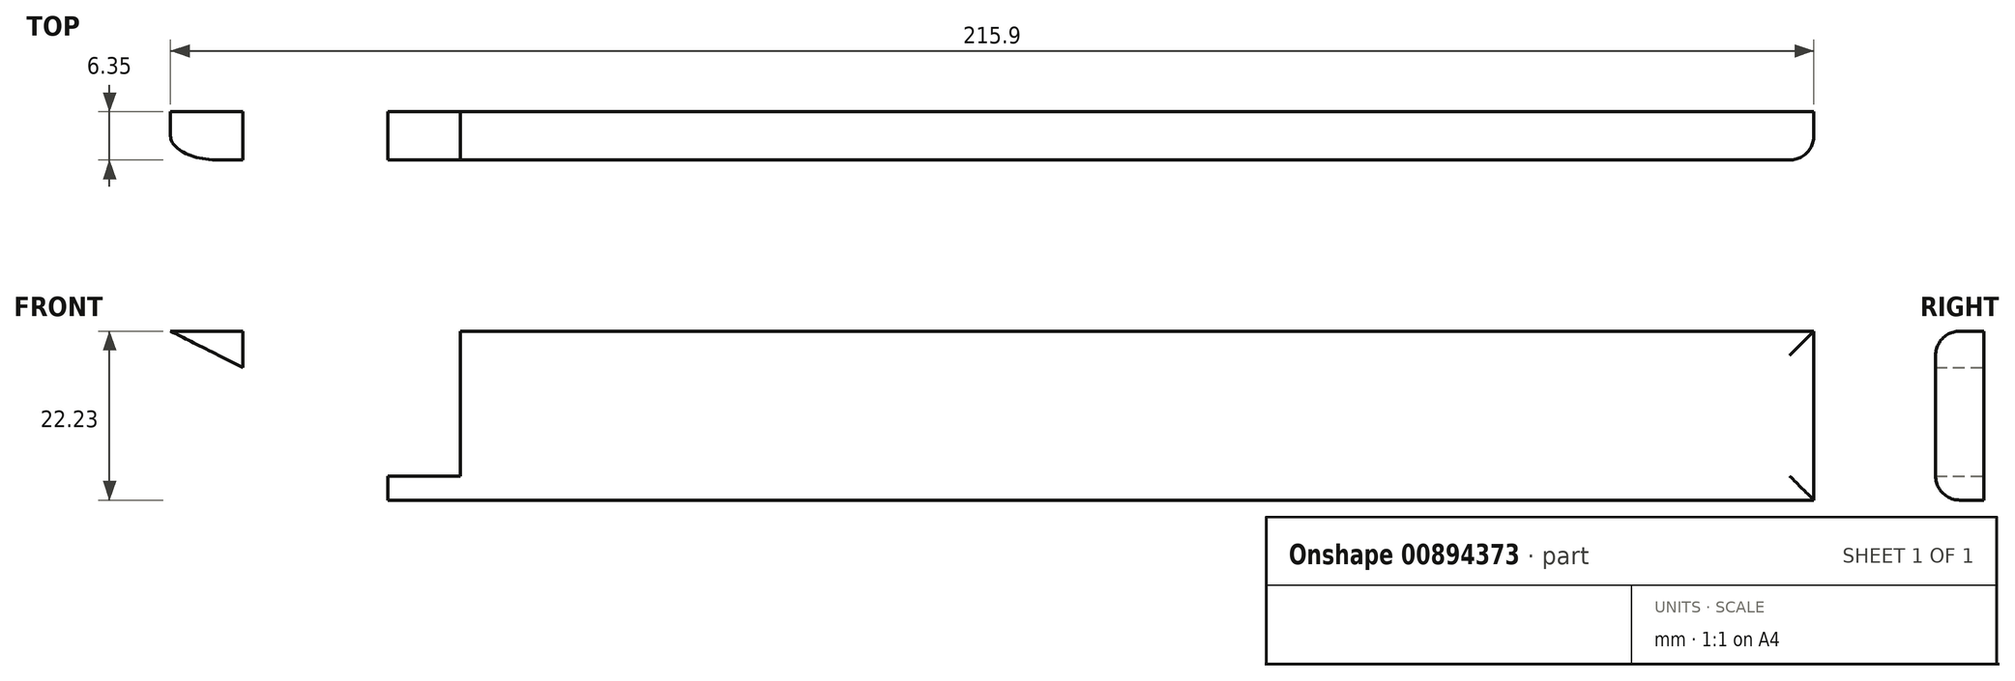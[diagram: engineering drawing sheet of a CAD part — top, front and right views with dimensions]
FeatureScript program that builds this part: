
annotation { "Feature Type Name" : "Feature", "Feature Type Description" : "" }
export const myFeature = defineFeature(function(context is Context, id is Id, definition is map)
    precondition{}
    {
        {
            var Q0;
            Q0=qCreatedBy(makeId("Front.planeOp"),FACE);
            var sketch = newSketch(context, id + "F0", { "sketchPlane" : qUnion([Q0])});
            skLineSegment(sketch, "E0.bottom", {"start": v(47.57, 0.5) * mm, "end": v(225.37, 0.5) * mm});
            skLineSegment(sketch, "E0.top", {"start": v(47.57, 22.73) * mm, "end": v(225.37, 22.73) * mm});
            skLineSegment(sketch, "E0.left", {"start": v(47.57, 0.5) * mm, "end": v(47.57, 22.73) * mm});
            skLineSegment(sketch, "E0.right", {"start": v(225.37, 0.5) * mm, "end": v(225.37, 22.73) * mm});
            skLineSegment(sketch, "E1.bottom", {"start": v(47.57, 0.5) * mm, "end": v(9.47, 0.5) * mm});
            skLineSegment(sketch, "E1.top", {"start": v(47.57, 22.73) * mm, "end": v(9.47, 22.73) * mm});
            skLineSegment(sketch, "E2.left", {"start": v(9.47, 0.5) * mm, "end": v(9.47, -2.42) * mm});
            skLineSegment(sketch, "E2.right", {"start": v(-155.63, 0.5) * mm, "end": v(-155.63, -59.94) * mm});
            skArc(sketch, "E3", {"start": v(9.47, 0.5) * mm, "mid": v(-4.22, -17.23) * mm, "end": v(-11.89, -38.28) * mm});
            skArc(sketch, "E4", {"start": v(-38.43, -17.23) * mm, "mid": v(-28.48, -31.94) * mm, "end": v(-11.89, -38.28) * mm});
            skPoint(sketch, "E4.startSnap0", {"position": v(-4.22, -17.23) * mm});
            skArc(sketch, "E5", {"start": v(9.47, 22.73) * mm, "mid": v(-1.4, 20.26) * mm, "end": v(-10.13, 13.34) * mm});
            skArc(sketch, "E6", {"start": v(-155.63, -59.94) * mm, "mid": v(-95.28, -43.39) * mm, "end": v(-38.43, -17.23) * mm});
            skArc(sketch, "E7", {"start": v(-97.34, 6.63) * mm, "mid": v(-126.55, 4.14) * mm, "end": v(-155.63, 0.5) * mm});
            skArc(sketch, "E8.0", {"start": v(-51.22, -4.45) * mm, "mid": v(-97.17, -6.09) * mm, "end": v(-142.93, -10.57) * mm});
            skArc(sketch, "E8.1", {"start": v(-50.24, -9.24) * mm, "mid": v(-50.54, -6.8) * mm, "end": v(-51.22, -4.45) * mm});
            skArc(sketch, "E8.2", {"start": v(-142.93, -44.3) * mm, "mid": v(-95.4, -29.88) * mm, "end": v(-50.24, -9.24) * mm});
            skLineSegment(sketch, "E8.3", {"start": v(-142.93, -10.57) * mm, "end": v(-142.93, -44.3) * mm});
            skPoint(sketch, "E9", {"position": v(38.04, 3.68) * mm});
            skLineSegment(sketch, "E10", {"start": v(38.04, 3.68) * mm, "end": v(38.04, 0.5) * mm});
            skLineSegment(sketch, "E11", {"start": v(38.04, 3.68) * mm, "end": v(47.57, 3.68) * mm});
            skLineSegment(sketch, "E12", {"start": v(9.47, 22.73) * mm, "end": v(17.79, 22.73) * mm});
            skLineSegment(sketch, "E13", {"start": v(9.47, 22.73) * mm, "end": v(19, 22.73) * mm});
            skLineSegment(sketch, "E14", {"start": v(19, 22.73) * mm, "end": v(19, 17.97) * mm});
            skLineSegment(sketch, "E15", {"start": v(19, 17.97) * mm, "end": v(9.47, 22.73) * mm});
            skFitSpline(sketch, "E16", {"points": [v(-10.13, 13.34) * mm, v(-24.5, 0) * mm, v(-55.64, 8.21) * mm], "startDerivative": vector(-27.78, -40.13) * mm, "endDerivative": vector(-61.83, 26.33) * mm});
            skFitSpline(sketch, "E17", {"points": [v(-40.15, 1.98) * mm, v(-66.13, 8.03) * mm, v(-97.34, 6.63) * mm], "startDerivative": vector(-52.72, 15.41) * mm, "endDerivative": vector(-61.46, -7.14) * mm});
            skSolve(sketch);
        }
        {
            var Q0;
            {var subQ3=sQuery(id+"F0.wireOp",EDGE,"E1.top");Q0=makeQuery(id+"F0.imprint","IMPRINT",FACE,{"disambiguationData":[TD([[makeQuery(id+"F0.imprint","IMPRINT",EDGE,{"derivedFrom":subQ3}),1.0]])]});}
            var Q1;
            {var subQ1=sQuery(id+"F0.wireOp",EDGE,"E0.bottom");Q1=makeQuery(id+"F0.imprint","IMPRINT",FACE,{"disambiguationData":[TD([[makeQuery(id+"F0.imprint","IMPRINT",EDGE,{"derivedFrom":subQ1}),1.0]])]});}
            var Q2;
            {var subQ3=sQuery(id+"F0.wireOp",EDGE,"E10");Q2=makeQuery(id+"F0.imprint","IMPRINT",FACE,{"disambiguationData":[TD([[makeQuery(id+"F0.imprint","IMPRINT",EDGE,{"derivedFrom":subQ3}),1.0]])]});}
            extrude(context, id + "F1", {"entities" : qUnion([Q0, Q1, Q2]), "depth" : 6.35 * mm, "offsetDistance" : 25.4 * mm});
        }
        {
            var Q0;
            Q0=makeQuery(id+"F1.opExtrude","CAP_FACE",FACE,{"disambiguationData":[OSD([sQuery(id+"F0.wireOp",EDGE,"E0.bottom"),sQuery(id+"F0.wireOp",EDGE,"E0.top"),sQuery(id+"F0.wireOp",EDGE,"E0.right"),sQuery(id+"F0.wireOp",EDGE,"E1.bottom"),sQuery(id+"F0.wireOp",EDGE,"E1.top"),sQuery(id+"F0.wireOp",EDGE,"E2.right"),sQuery(id+"F0.wireOp",EDGE,"E3"),sQuery(id+"F0.wireOp",EDGE,"E4"),sQuery(id+"F0.wireOp",EDGE,"E5"),sQuery(id+"F0.wireOp",EDGE,"E6"),sQuery(id+"F0.wireOp",EDGE,"E7"),sQuery(id+"F0.wireOp",EDGE,"E8.0"),sQuery(id+"F0.wireOp",EDGE,"E8.1"),sQuery(id+"F0.wireOp",EDGE,"E8.2"),sQuery(id+"F0.wireOp",EDGE,"E8.3"),sQuery(id+"F0.wireOp",EDGE,"E14"),sQuery(id+"F0.wireOp",EDGE,"E15"),sQuery(id+"F0.wireOp",EDGE,"E16"),sQuery(id+"F0.wireOp",EDGE,"E17")])],"isStart":false});
            var sketch = newSketch(context, id + "F2", { "sketchPlane" : qUnion([Q0])});
            skLineSegment(sketch, "E18", {"start": v(9.47, 0.5) * mm, "end": v(47.57, 0.5) * mm});
            skLineSegment(sketch, "E19", {"start": v(47.57, 0.5) * mm, "end": v(47.57, 3.68) * mm});
            skLineSegment(sketch, "E20", {"start": v(47.57, 3.68) * mm, "end": v(38.04, 3.68) * mm});
            skPoint(sketch, "E21", {"position": v(38.04, 3.68) * mm});
            skSolve(sketch);
        }
        {
            var Q0;
            Q0=sQuery(id+"F2.wireOp",VERTEX,"E20.end");
            var Q1;
            Q1=makeQuery(id+"F1.opExtrude","SWEPT_BODY",BODY,{"disambiguationData":[OSD([sQuery(id+"F0.wireOp",EDGE,"E0.bottom"),sQuery(id+"F0.wireOp",EDGE,"E0.top"),sQuery(id+"F0.wireOp",EDGE,"E0.right"),sQuery(id+"F0.wireOp",EDGE,"E1.bottom"),sQuery(id+"F0.wireOp",EDGE,"E1.top"),sQuery(id+"F0.wireOp",EDGE,"E2.right"),sQuery(id+"F0.wireOp",EDGE,"E3"),sQuery(id+"F0.wireOp",EDGE,"E4"),sQuery(id+"F0.wireOp",EDGE,"E5"),sQuery(id+"F0.wireOp",EDGE,"E6"),sQuery(id+"F0.wireOp",EDGE,"E7"),sQuery(id+"F0.wireOp",EDGE,"E8.0"),sQuery(id+"F0.wireOp",EDGE,"E8.1"),sQuery(id+"F0.wireOp",EDGE,"E8.2"),sQuery(id+"F0.wireOp",EDGE,"E8.3"),sQuery(id+"F0.wireOp",EDGE,"E14"),sQuery(id+"F0.wireOp",EDGE,"E15"),sQuery(id+"F0.wireOp",EDGE,"E16"),sQuery(id+"F0.wireOp",EDGE,"E17")])]});
            hole(context, id + "F3", {"style" : HoleStyle.SIMPLE, "endStyle" : HoleEndStyle.BLIND, "holeDiameter" : 2.38 * mm, "majorDiameter" : 6.35 * mm, "holeDepth" : 6.35 * mm, "isTappedThrough" : true, "tappedDepth" : 12.7 * mm, "tapClearance" : 3, "locations" : qUnion([Q0]), "scope" : qUnion([Q1])});
        }
        {
            var Q0;
            Q0=makeQuery(id+"F1.opExtrude","CAP_EDGE",EDGE,{"disambiguationData":[OSD([sQuery(id+"F0.wireOp",EDGE,"E6")])],"isStart":false});
            var Q1;
            Q1=makeQuery(id+"F1.opExtrude","CAP_EDGE",EDGE,{"disambiguationData":[OSD([sQuery(id+"F0.wireOp",EDGE,"E2.right")])],"isStart":false});
            var Q2;
            Q2=makeQuery(id+"F1.opExtrude","CAP_EDGE",EDGE,{"disambiguationData":[OSD([sQuery(id+"F0.wireOp",EDGE,"E7")])],"isStart":false});
            var Q3;
            Q3=makeQuery(id+"F1.opExtrude","CAP_EDGE",EDGE,{"disambiguationData":[OSD([sQuery(id+"F0.wireOp",EDGE,"E8.0")])],"isStart":false});
            var Q4;
            Q4=makeQuery(id+"F1.opExtrude","CAP_EDGE",EDGE,{"disambiguationData":[OSD([sQuery(id+"F0.wireOp",EDGE,"E8.3")])],"isStart":false});
            var Q5;
            Q5=makeQuery(id+"F1.opExtrude","CAP_EDGE",EDGE,{"disambiguationData":[OSD([sQuery(id+"F0.wireOp",EDGE,"E8.2")])],"isStart":false});
            var Q6;
            Q6=makeQuery(id+"F1.opExtrude","CAP_EDGE",EDGE,{"disambiguationData":[OSD([sQuery(id+"F0.wireOp",EDGE,"E8.1")])],"isStart":false});
            var Q7;
            Q7=makeQuery(id+"F1.opExtrude","CAP_EDGE",EDGE,{"disambiguationData":[OSD([sQuery(id+"F0.wireOp",EDGE,"E17")])],"isStart":false});
            var Q8;
            Q8=makeQuery(id+"F1.opExtrude","CAP_EDGE",EDGE,{"disambiguationData":[OSD([sQuery(id+"F0.wireOp",EDGE,"E16")])],"isStart":false});
            var Q9;
            Q9=makeQuery(id+"F1.opExtrude","CAP_EDGE",EDGE,{"disambiguationData":[OSD([sQuery(id+"F0.wireOp",EDGE,"E4")])],"isStart":false});
            var Q10;
            Q10=makeQuery(id+"F1.opExtrude","CAP_EDGE",EDGE,{"disambiguationData":[OSD([sQuery(id+"F0.wireOp",EDGE,"E3")])],"isStart":false});
            var Q11;
            Q11=makeQuery(id+"F1.opExtrude","CAP_EDGE",EDGE,{"disambiguationData":[OSD([sQuery(id+"F0.wireOp",EDGE,"E5")])],"isStart":false});
            var Q12;
            Q12=makeQuery(id+"F1.opExtrude","CAP_EDGE",EDGE,{"disambiguationData":[OSD([sQuery(id+"F0.wireOp",EDGE,"E0.top"),sQuery(id+"F0.wireOp",EDGE,"E1.top")])],"isStart":false});
            var Q13;
            Q13=makeQuery(id+"F1.opExtrude","CAP_EDGE",EDGE,{"disambiguationData":[OSD([sQuery(id+"F0.wireOp",EDGE,"E0.bottom"),sQuery(id+"F0.wireOp",EDGE,"E1.bottom")])],"isStart":false});
            var Q14;
            Q14=makeQuery(id+"F1.opExtrude","CAP_EDGE",EDGE,{"disambiguationData":[OSD([sQuery(id+"F0.wireOp",EDGE,"E0.right")])],"isStart":false});
            fillet(context, id + "F4", {"entities" : qUnion([Q0, Q1, Q2, Q3, Q4, Q5, Q6, Q7, Q8, Q9, Q10, Q11, Q12, Q13, Q14]), "tangentPropagation" : true, "radius" : 3.17 * mm, "defaultsChanged" : true, "vertexSettings" : [], "allowEdgeOverflow" : false});
        }
    });
